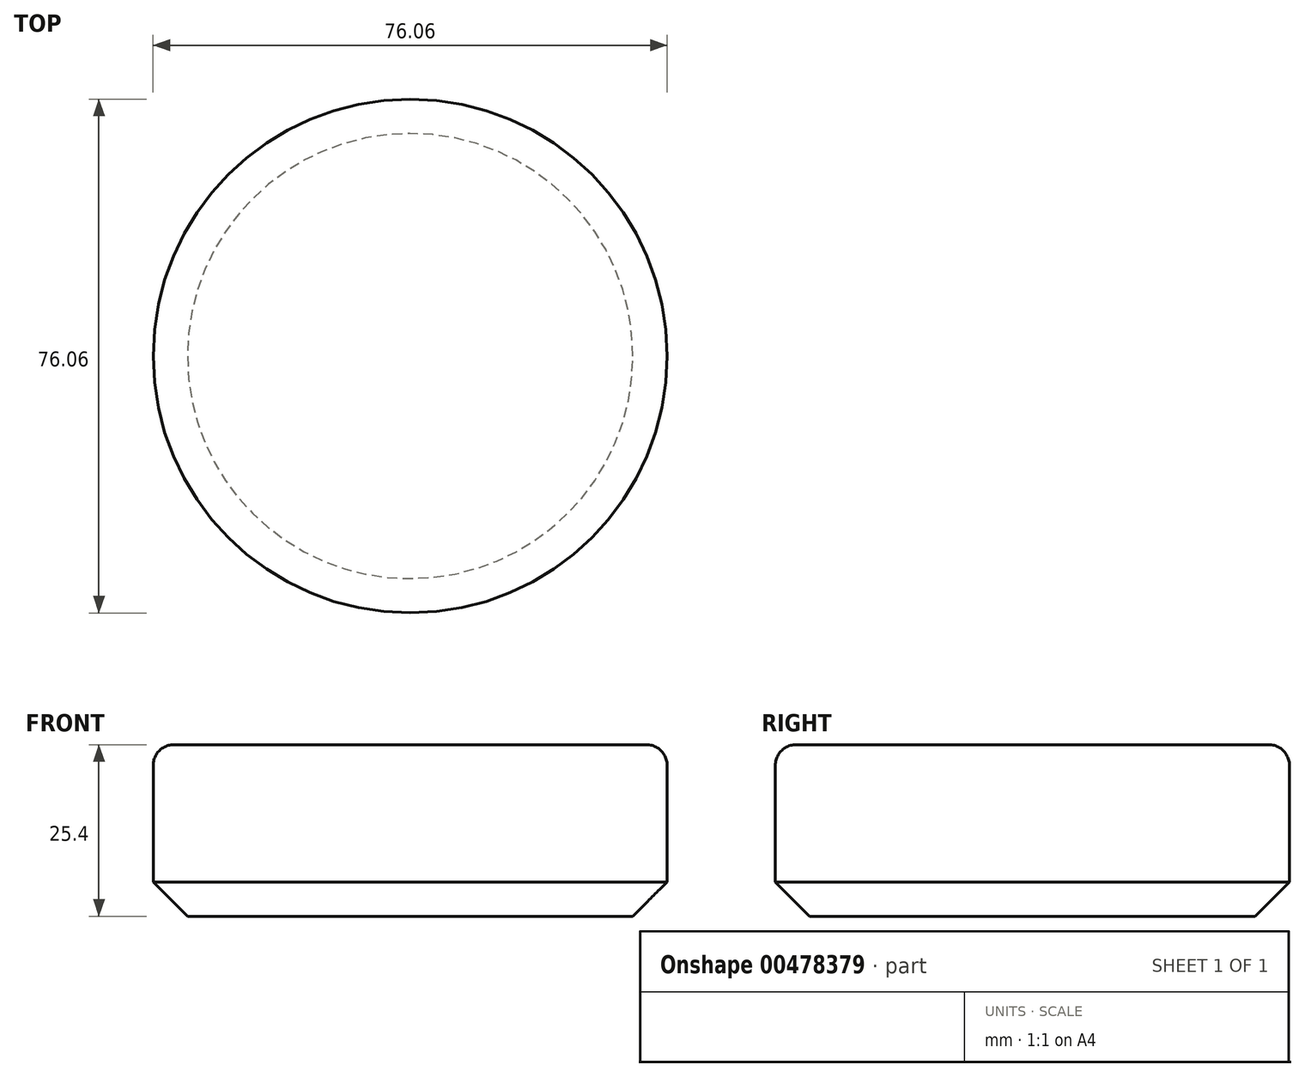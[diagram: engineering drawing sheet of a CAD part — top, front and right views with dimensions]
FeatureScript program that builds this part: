
annotation { "Feature Type Name" : "Feature", "Feature Type Description" : "" }
export const myFeature = defineFeature(function(context is Context, id is Id, definition is map)
    precondition{}
    {
        {
            var Q0;
            Q0=qCreatedBy(makeId("Top.planeOp"),FACE);
            var sketch = newSketch(context, id + "F0", { "sketchPlane" : qUnion([Q0])});
            skCircle(sketch, "E0", {"center": v(0, 0) * mm, "radius": 38.03 * mm});
            skSolve(sketch);
        }
        {
            var Q0;
            Q0 = qSketchRegion(id + "F0", true);
            extrude(context, id + "F1", {"entities" : qUnion([Q0]), "depth" : 25.4 * mm});
        }
        {
            var Q0;
            Q0=makeQuery(id+"F1.opExtrude","CAP_FACE",FACE,{"disambiguationData":[OSD([sQuery(id+"F0.wireOp",EDGE,"E0")])],"isStart":false});
            var Q1;
            Q1=makeQuery(id+"F1.opExtrude","CAP_EDGE",EDGE,{"disambiguationData":[OSD([sQuery(id+"F0.wireOp",EDGE,"E0")])],"isStart":false});
            fillet(context, id + "F2", {"entities" : qUnion([Q0, Q1]), "radius" : 3.07 * mm, "tangentPropagation" : true, "allowEdgeOverflow" : false});
        }
        {
            var Q0;
            Q0=makeQuery(id+"F1.opExtrude","CAP_EDGE",EDGE,{"disambiguationData":[OSD([sQuery(id+"F0.wireOp",EDGE,"E0")])],"isStart":true});
            chamfer(context, id + "F3", {"entities" : qUnion([Q0]), "width" : 5.08 * mm, "tangentPropagation" : true});
        }
    });
